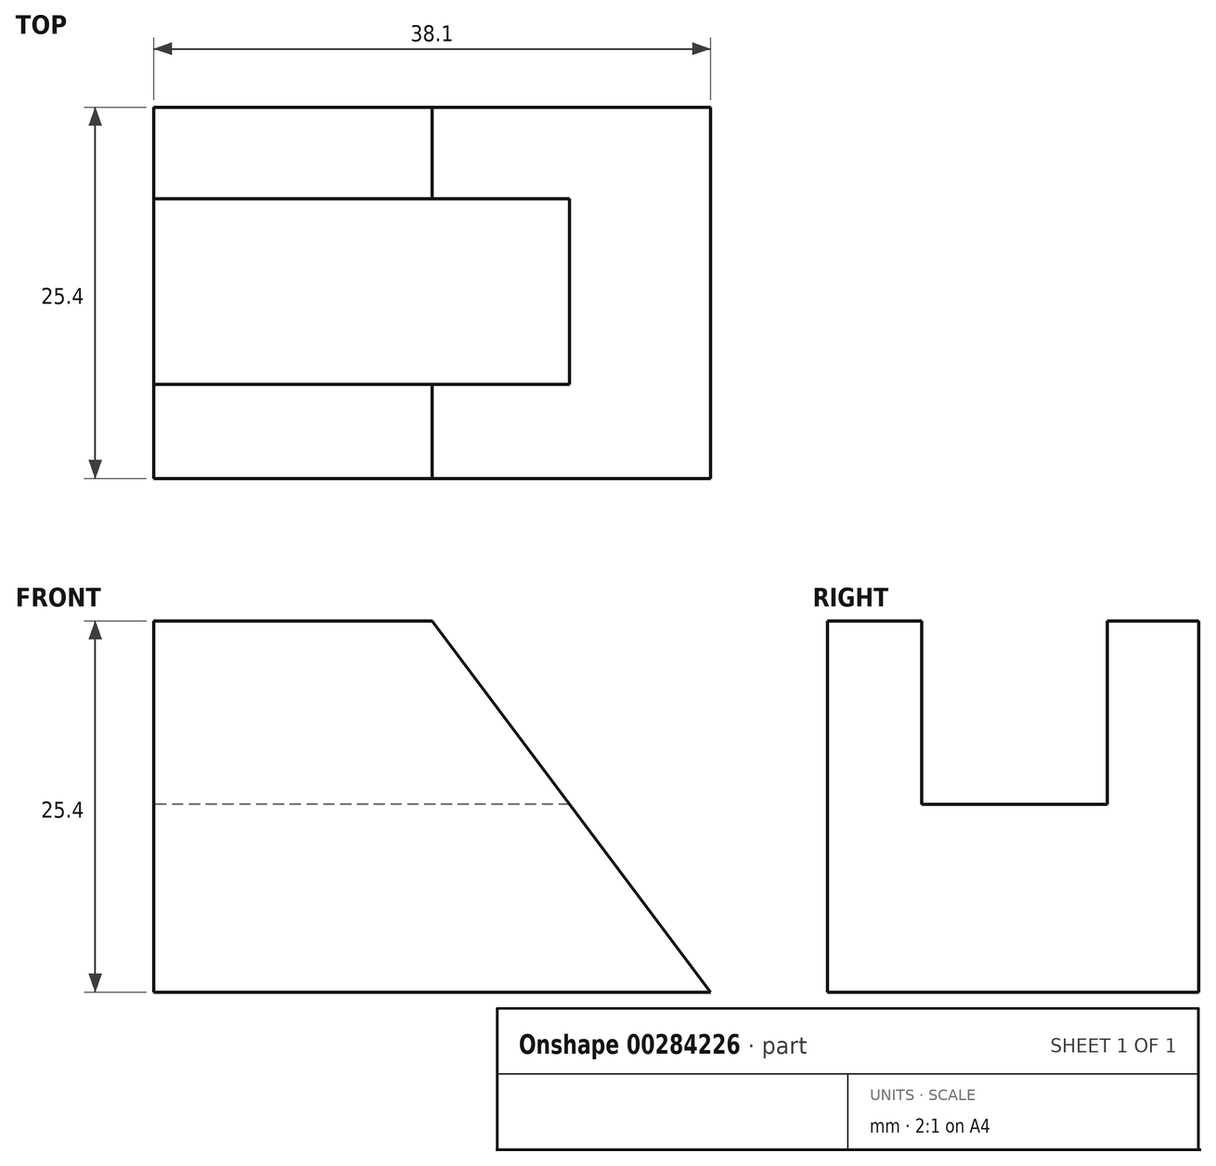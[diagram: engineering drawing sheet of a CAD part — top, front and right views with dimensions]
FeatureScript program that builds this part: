
annotation { "Feature Type Name" : "Feature", "Feature Type Description" : "" }
export const myFeature = defineFeature(function(context is Context, id is Id, definition is map)
    precondition{}
    {
        {
            var Q0;
            Q0=qCreatedBy(makeId("Front.planeOp"),FACE);
            var sketch = newSketch(context, id + "F0", { "sketchPlane" : qUnion([Q0])});
            skLineSegment(sketch, "E0", {"start": v(0, 0) * mm, "end": v(0, 25.4) * mm});
            skLineSegment(sketch, "E1", {"start": v(0, 25.4) * mm, "end": v(19.05, 25.4) * mm});
            skLineSegment(sketch, "E2", {"start": v(19.05, 25.4) * mm, "end": v(38.1, 0) * mm});
            skLineSegment(sketch, "E3", {"start": v(38.1, 0) * mm, "end": v(0, 0) * mm});
            skSolve(sketch);
        }
        {
            var Q0;
            Q0 = qSketchRegion(id + "F0", true);
            extrude(context, id + "F1", {"entities" : qUnion([Q0]), "depth" : 25.4 * mm});
        }
        {
            var Q0;
            Q0=qCreatedBy(makeId("Right.planeOp"),FACE);
            var sketch = newSketch(context, id + "F2", { "sketchPlane" : qUnion([Q0])});
            skLineSegment(sketch, "E4", {"start": v(-6.27, 25.55) * mm, "end": v(-6.27, 12.85) * mm});
            skLineSegment(sketch, "E5", {"start": v(-6.27, 12.85) * mm, "end": v(-18.97, 12.85) * mm});
            skLineSegment(sketch, "E6", {"start": v(-18.97, 12.85) * mm, "end": v(-18.97, 25.55) * mm});
            skLineSegment(sketch, "E7", {"start": v(-18.97, 25.55) * mm, "end": v(-6.27, 25.55) * mm});
            skSolve(sketch);
        }
        {
            var Q0;
            Q0=makeQuery(id+"F2.imprint","IMPRINT",FACE,{"disambiguationData":[TD([[makeQuery(id+"F2.imprint","IMPRINT",EDGE,{"derivedFrom":sQuery(id+"F2.wireOp",EDGE,"E4")}),-1.0]])]});
            extrude(context, id + "F3", {"entities" : qUnion([Q0]), "operationType" : NewBodyOperationType.REMOVE, "depth" : 38.1 * mm});
        }
    });
